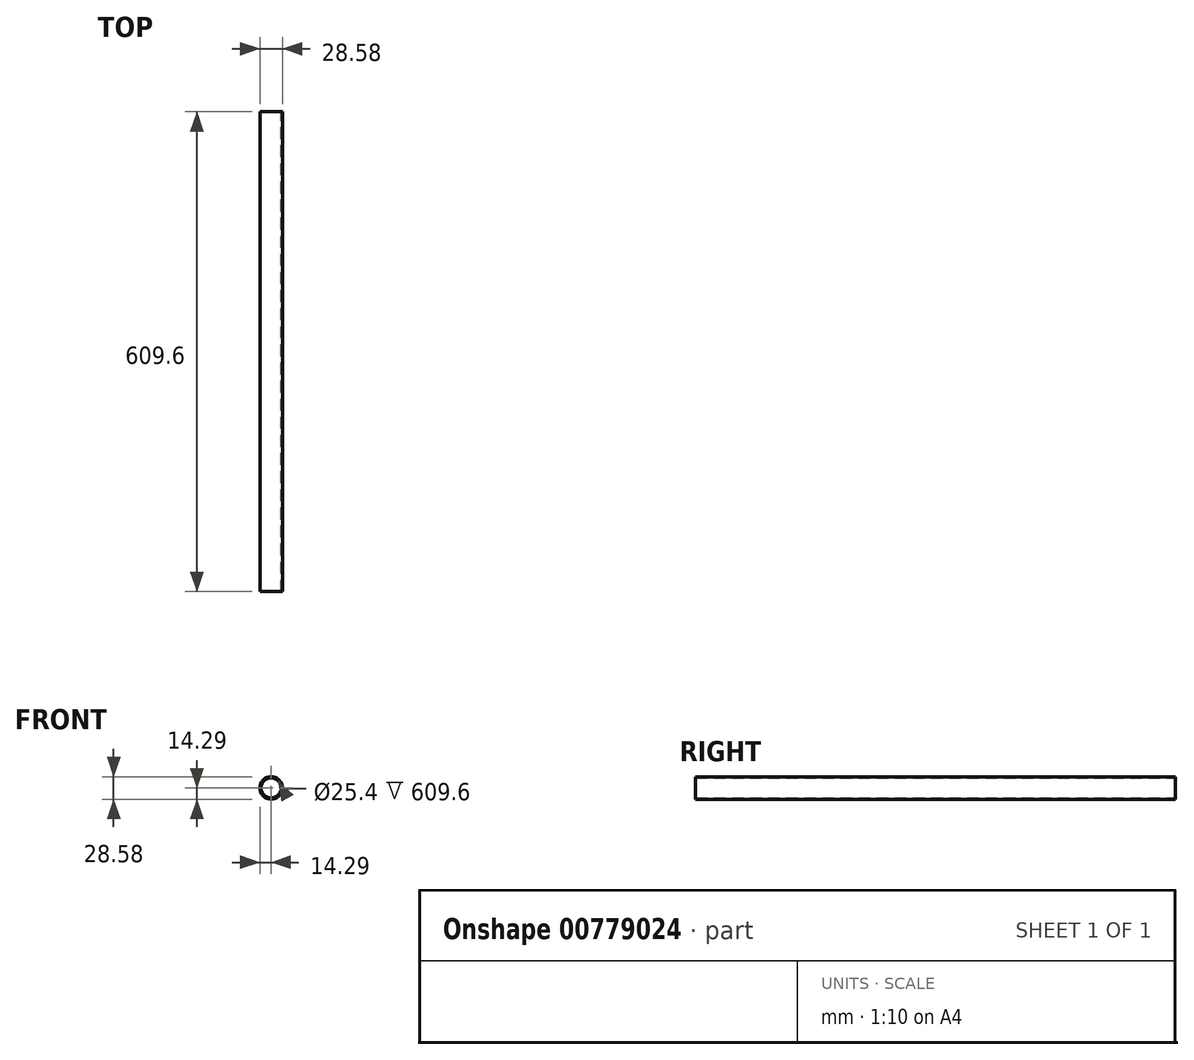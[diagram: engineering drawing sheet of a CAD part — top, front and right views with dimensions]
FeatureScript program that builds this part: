
annotation { "Feature Type Name" : "Feature", "Feature Type Description" : "" }
export const myFeature = defineFeature(function(context is Context, id is Id, definition is map)
    precondition{}
    {
        {
            var Q0;
            Q0=qCreatedBy(makeId("Front.planeOp"),FACE);
            var sketch = newSketch(context, id + "F0", { "sketchPlane" : qUnion([Q0])});
            skCircle(sketch, "E0", {"center": v(0, 0) * mm, "radius": 14.29 * mm});
            skCircle(sketch, "E1", {"center": v(0, 0) * mm, "radius": 12.7 * mm});
            skSolve(sketch);
        }
        {
            var Q0;
            Q0 = qSketchRegion(id + "F0", true);
            extrude(context, id + "F1", {"entities" : qUnion([Q0]), "depth" : 609.6 * mm, "offsetDistance" : 25.4 * mm});
        }
    });
